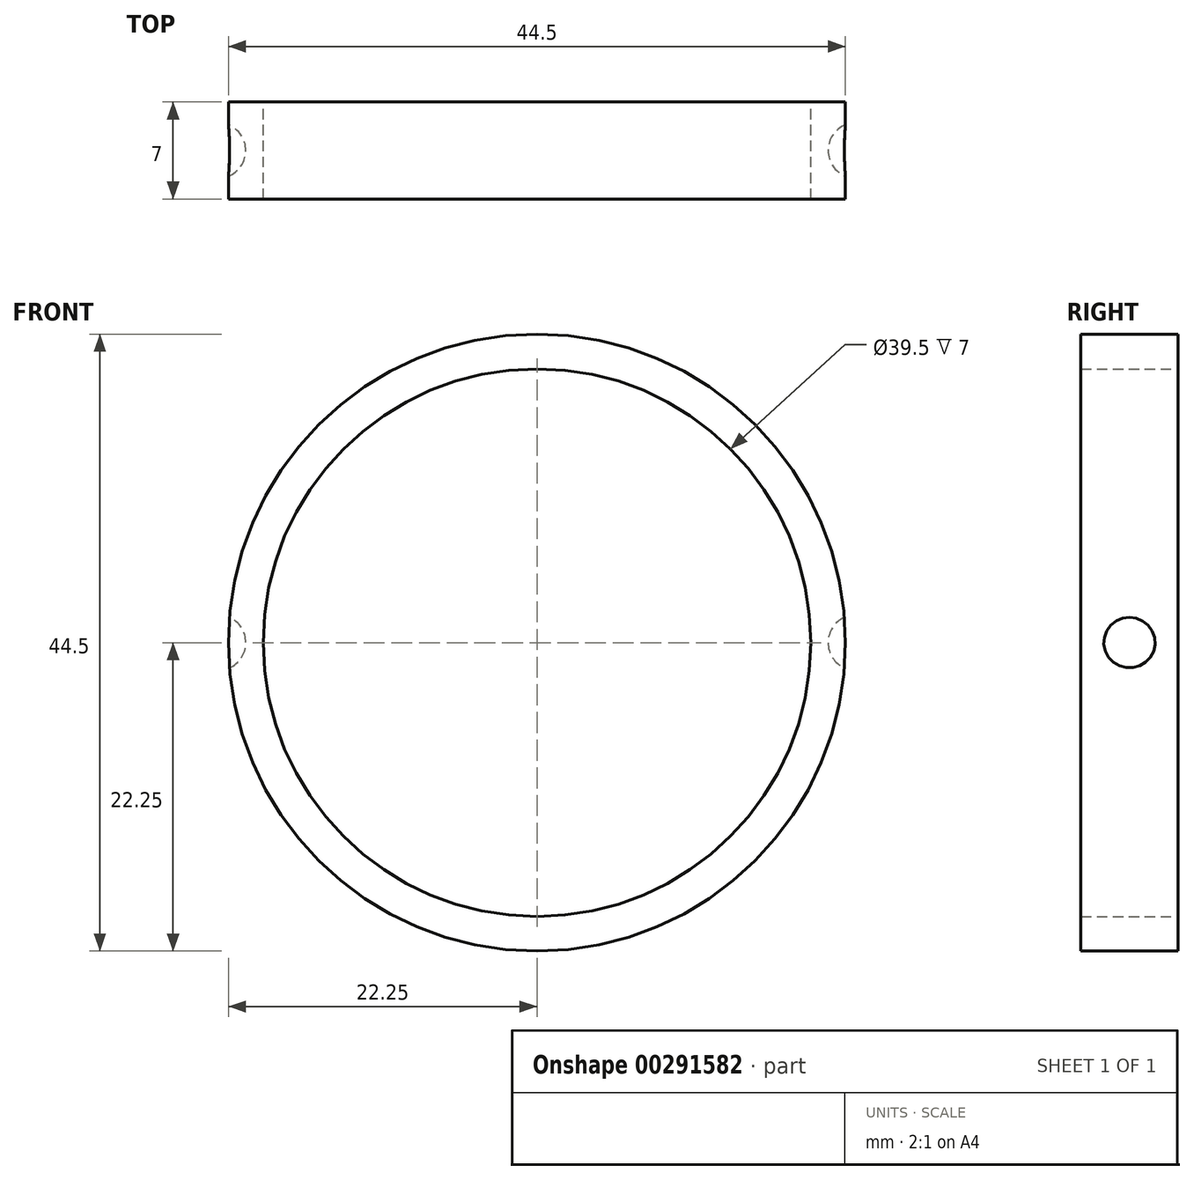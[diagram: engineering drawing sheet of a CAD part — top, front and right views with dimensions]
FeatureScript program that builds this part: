
annotation { "Feature Type Name" : "Feature", "Feature Type Description" : "" }
export const myFeature = defineFeature(function(context is Context, id is Id, definition is map)
    precondition{}
    {
        {
            var Q0;
            Q0=qCreatedBy(makeId("Front.planeOp"),FACE);
            var sketch = newSketch(context, id + "F0", { "sketchPlane" : qUnion([Q0])});
            skCircle(sketch, "E0", {"center": v(0, 0) * mm, "radius": 22.25 * mm});
            skCircle(sketch, "E1", {"center": v(0, 0) * mm, "radius": 19.75 * mm});
            skSolve(sketch);
        }
        {
            var Q0;
            Q0=makeQuery(id+"F0.imprint","IMPRINT",FACE,{"disambiguationData":[TD([[makeQuery(id+"F0.imprint","IMPRINT",EDGE,{"derivedFrom":sQuery(id+"F0.wireOp",EDGE,"E0")}),1.0]])]});
            extrude(context, id + "F1", {"entities" : qUnion([Q0]), "depth" : 7 * mm});
        }
        {
            var Q0;
            Q0=qCreatedBy(makeId("Top.planeOp"),FACE);
            cPlane(context, id + "F2", {"entities" : qUnion([Q0]), "cplaneType" : CPlaneType.OFFSET, "offset" : 20.3 * mm, "width" : 150 * mm, "height" : 150 * mm});
        }
        {
            var Q0;
            Q0=qCreatedBy(id+"F2.planeOp",FACE);
            var sketch = newSketch(context, id + "F3", { "sketchPlane" : qUnion([Q0])});
            skArc(sketch, "E2", {"start": v(0, -1.5) * mm, "mid": v(-2, -3.5) * mm, "end": v(0, -5.5) * mm});
            skLineSegment(sketch, "E3", {"start": v(0, -7) * mm, "end": v(0, 0) * mm});
            skSolve(sketch);
        }
        {
            var Q0;
            Q0=sQuery(id+"F3.wireOp",EDGE,"E2");
            var Q1;
            Q1=sQuery(id+"F3.wireOp",EDGE,"E3");
            revolve(context, id + "F4", {"bodyType" : ToolBodyType.SURFACE, "surfaceEntities" : qUnion([Q0]), "axis" : qUnion([Q1]), "revolveType" : RevolveType.FULL});
        }
        {
            var Q0;
            Q0=makeQuery(id+"F4.opRevolve","SWEPT_BODY",BODY,{"disambiguationData":[OSD([sQuery(id+"F3.wireOp",EDGE,"E2")])]});
            var Q1;
            Q1=qCreatedBy(makeId("Top.planeOp"),FACE);
            mirror(context, id + "F5", {"entities" : qUnion([Q0]), "mirrorPlane" : qUnion([Q1])});
        }
        {
            var Q0;
            Q0=qCreatedBy(makeId("Right.planeOp"),FACE);
            cPlane(context, id + "F6", {"entities" : qUnion([Q0]), "cplaneType" : CPlaneType.OFFSET, "offset" : 23 * mm, "width" : 150 * mm, "height" : 150 * mm});
        }
        {
            var Q0;
            Q0=qCreatedBy(id+"F6.planeOp",FACE);
            var sketch = newSketch(context, id + "F7", { "sketchPlane" : qUnion([Q0])});
            skArc(sketch, "E4", {"start": v(-1.5, 0) * mm, "mid": v(-3.5, 2) * mm, "end": v(-5.5, 0) * mm});
            skLineSegment(sketch, "E5", {"start": v(0, 0) * mm, "end": v(-6.98, 0) * mm});
            skSolve(sketch);
        }
        {
            var Q0;
            {var subQ0=sQuery(id+"F7.wireOp",EDGE,"E4");Q0=makeQuery(id+"F7.imprint","IMPRINT",FACE,{"disambiguationData":[TD([[makeQuery(id+"F7.imprint","IMPRINT",EDGE,{"derivedFrom":subQ0}),1.0]])]});}
            var Q1;
            Q1=sQuery(id+"F7.wireOp",EDGE,"E5");
            revolve(context, id + "F8", {"operationType" : NewBodyOperationType.REMOVE, "entities" : qUnion([Q0]), "axis" : qUnion([Q1]), "revolveType" : RevolveType.FULL, "oppositeDirection" : true});
        }
        {
            var Q0;
            Q0=makeQuery(id+"F1.opExtrude","SWEPT_BODY",BODY,{"disambiguationData":[OSD([sQuery(id+"F0.wireOp",EDGE,"E0"),sQuery(id+"F0.wireOp",EDGE,"E1")])]});
            var Q1;
            Q1=qCreatedBy(makeId("Right.planeOp"),FACE);
            mirror(context, id + "F9", {"operationType" : NewBodyOperationType.INTERSECT, "entities" : qUnion([Q0]), "mirrorPlane" : qUnion([Q1])});
        }
    });
